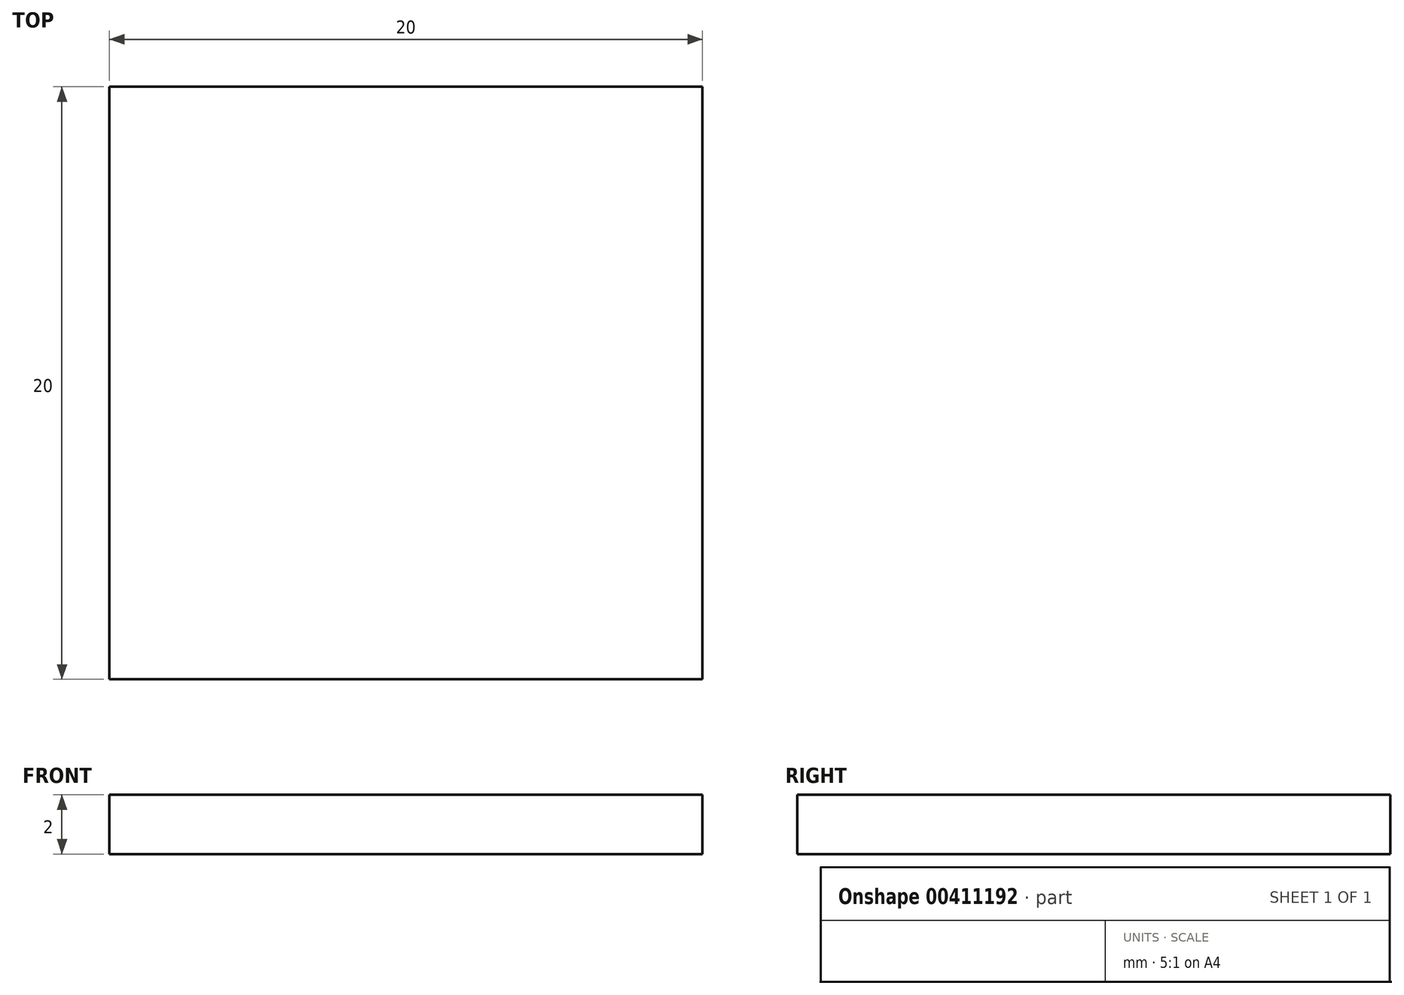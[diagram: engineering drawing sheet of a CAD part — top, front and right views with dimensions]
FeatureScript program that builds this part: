
annotation { "Feature Type Name" : "Feature", "Feature Type Description" : "" }
export const myFeature = defineFeature(function(context is Context, id is Id, definition is map)
    precondition{}
    {
        {
            var Q0;
            Q0=qCreatedBy(makeId("Top.planeOp"),FACE);
            var sketch = newSketch(context, id + "F0", { "sketchPlane" : qUnion([Q0])});
            skLineSegment(sketch, "E0.bottom", {"start": v(10, -10) * mm, "end": v(-10, -10) * mm});
            skLineSegment(sketch, "E0.top", {"start": v(10, 10) * mm, "end": v(-10, 10) * mm});
            skLineSegment(sketch, "E0.left", {"start": v(10, -10) * mm, "end": v(10, 10) * mm});
            skLineSegment(sketch, "E0.right", {"start": v(-10, -10) * mm, "end": v(-10, 10) * mm});
            skPoint(sketch, "E0.middle", {"position": v(0, 0) * mm});
            skSolve(sketch);
        }
        {
            var Q0;
            Q0 = qSketchRegion(id + "F0", true);
            extrude(context, id + "F1", {"entities" : qUnion([Q0]), "depth" : 2 * mm});
        }
    });
